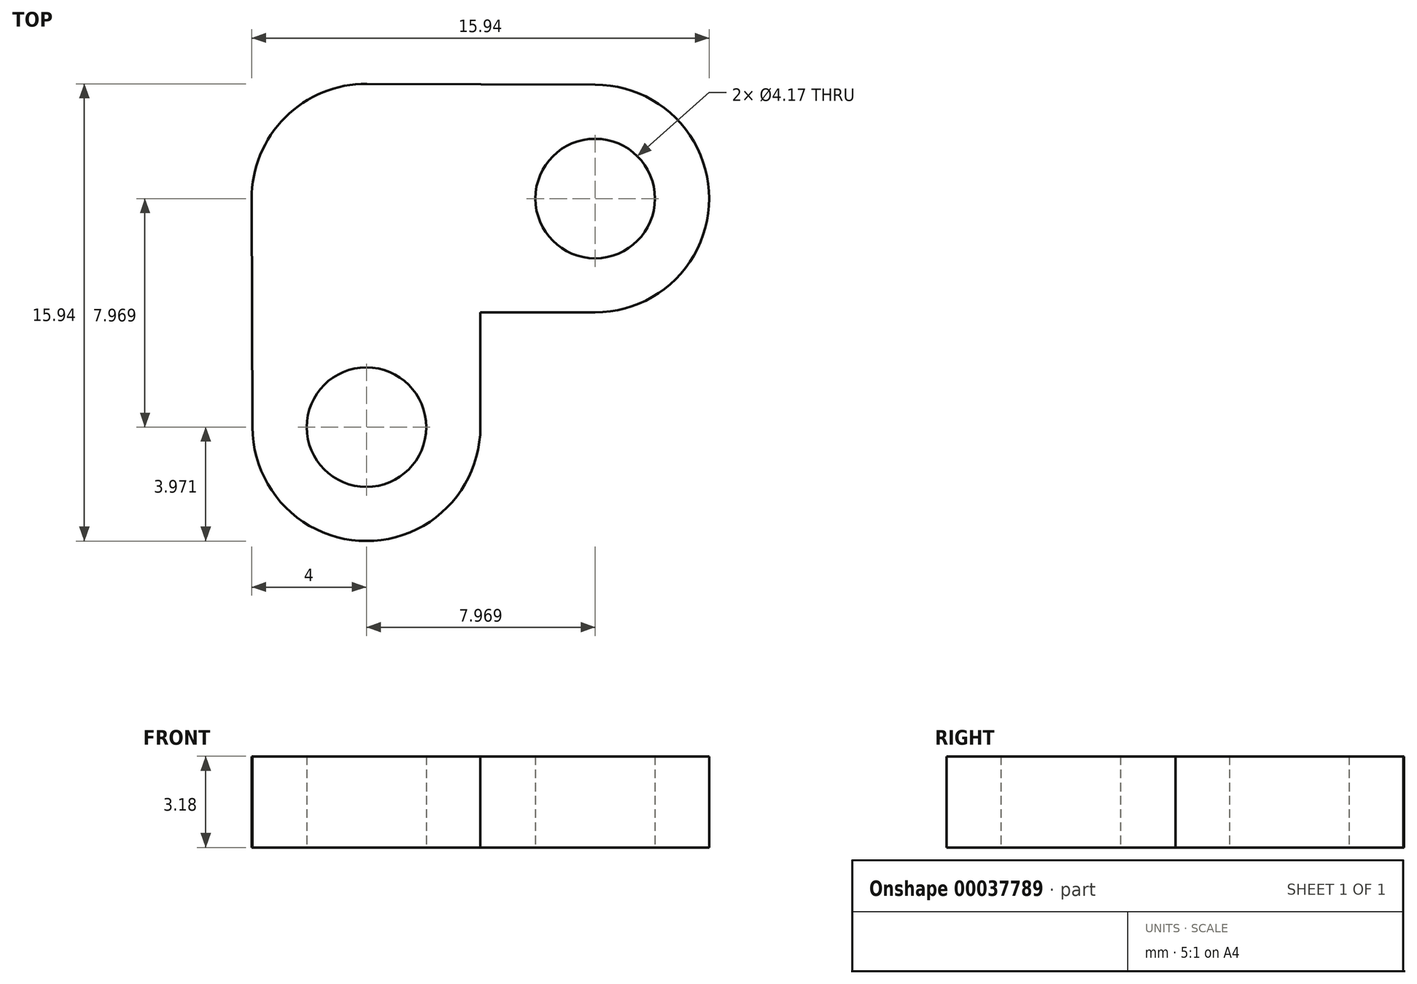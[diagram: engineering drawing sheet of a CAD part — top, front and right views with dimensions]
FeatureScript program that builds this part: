
annotation { "Feature Type Name" : "Feature", "Feature Type Description" : "" }
export const myFeature = defineFeature(function(context is Context, id is Id, definition is map)
    precondition{}
    {
        {
            var Q0;
            Q0=qCreatedBy(makeId("Top.planeOp"),FACE);
            var sketch = newSketch(context, id + "F0", { "sketchPlane" : qUnion([Q0])});
            skLineSegment(sketch, "E0", {"start": v(0, 0) * mm, "end": v(7.97, 0) * mm, "construction": true});
            skLineSegment(sketch, "E1", {"start": v(0, 0) * mm, "end": v(0, -7.97) * mm, "construction": true});
            skLineSegment(sketch, "E2", {"start": v(-3.97, -7.97) * mm, "end": v(3.97, -7.97) * mm, "construction": true});
            skLineSegment(sketch, "E3", {"start": v(7.97, 3.97) * mm, "end": v(7.97, -3.97) * mm, "construction": true});
            skArc(sketch, "E4", {"start": v(-4, -0.02) * mm, "mid": v(2.83, -2.83) * mm, "end": v(0.02, 4) * mm, "construction": true});
            skArc(sketch, "E5", {"start": v(7.97, 3.97) * mm, "mid": v(4, 0) * mm, "end": v(7.97, -3.97) * mm, "construction": true});
            skArc(sketch, "E6", {"start": v(0.02, 4) * mm, "mid": v(-2.83, 2.83) * mm, "end": v(-4, -0.02) * mm});
            skArc(sketch, "E7", {"start": v(7.97, -3.97) * mm, "mid": v(11.94, 0) * mm, "end": v(7.97, 3.97) * mm});
            skArc(sketch, "E8", {"start": v(-3.97, -7.97) * mm, "mid": v(0, -11.94) * mm, "end": v(3.97, -7.97) * mm});
            skLineSegment(sketch, "E9", {"start": v(3.97, -7.97) * mm, "end": v(3.97, -3.97) * mm});
            skLineSegment(sketch, "E10", {"start": v(7.97, -3.97) * mm, "end": v(3.97, -3.97) * mm});
            skLineSegment(sketch, "E11", {"start": v(-3.97, -7.97) * mm, "end": v(-4, -0.02) * mm});
            skLineSegment(sketch, "E12", {"start": v(7.97, 3.97) * mm, "end": v(0.02, 4) * mm});
            skCircle(sketch, "E13", {"center": v(0, -7.97) * mm, "radius": 2.08 * mm});
            skCircle(sketch, "E14", {"center": v(7.97, 0) * mm, "radius": 2.08 * mm});
            skSolve(sketch);
        }
        {
            var Q0;
            Q0 = qSketchRegion(id + "F0", true);
            extrude(context, id + "F1", {"entities" : qUnion([Q0]), "depth" : 3.17 * mm});
        }
    });
